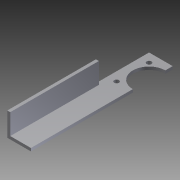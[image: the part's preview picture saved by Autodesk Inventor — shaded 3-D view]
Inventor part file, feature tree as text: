
AUTODESK INVENTOR PART (.ipt)
format: ipt  version: 2012 (Build 160160000, 160)  size: 106,496 bytes
history: native  units: in
note: dims shown in document units (in); Inventor stores cm internally (conversion verified against a paired STEP export)
features: other x3, extrude x3, sketch x3
ambient origin geometry x8: Origin, YZ Plane, XZ Plane, XY Plane, X Axis, Y Axis, Z Axis, Center Point
bodies: Solid1 (feature_tree)
feature tree (9):
  other  "8 ball corner L.ipt"
  extrude  "Extrusion1"  Depth=1.5in TaperAngle=0.0deg
  sketch  "Sketch3"  dims[d5=1.0in d6=0.125in d7=0.375in d8=0.375in d9=0.125in d10=0.0in d11=0.125in d12=0.0in]
  extrude  "Extrusion2"  Depth=0.375in
  extrude  "Extrusion3"  Depth=0.125in
  other  "Solid1::8 ball corner L.ipt"
  sketch  "Sketch1"  dims[d0=0.3937in d1=1.5in d2=0.0in]
  sketch  "Sketch2"  dims[d3=0.25in d4=0.375in]
  other  "TaggingFeature1"
